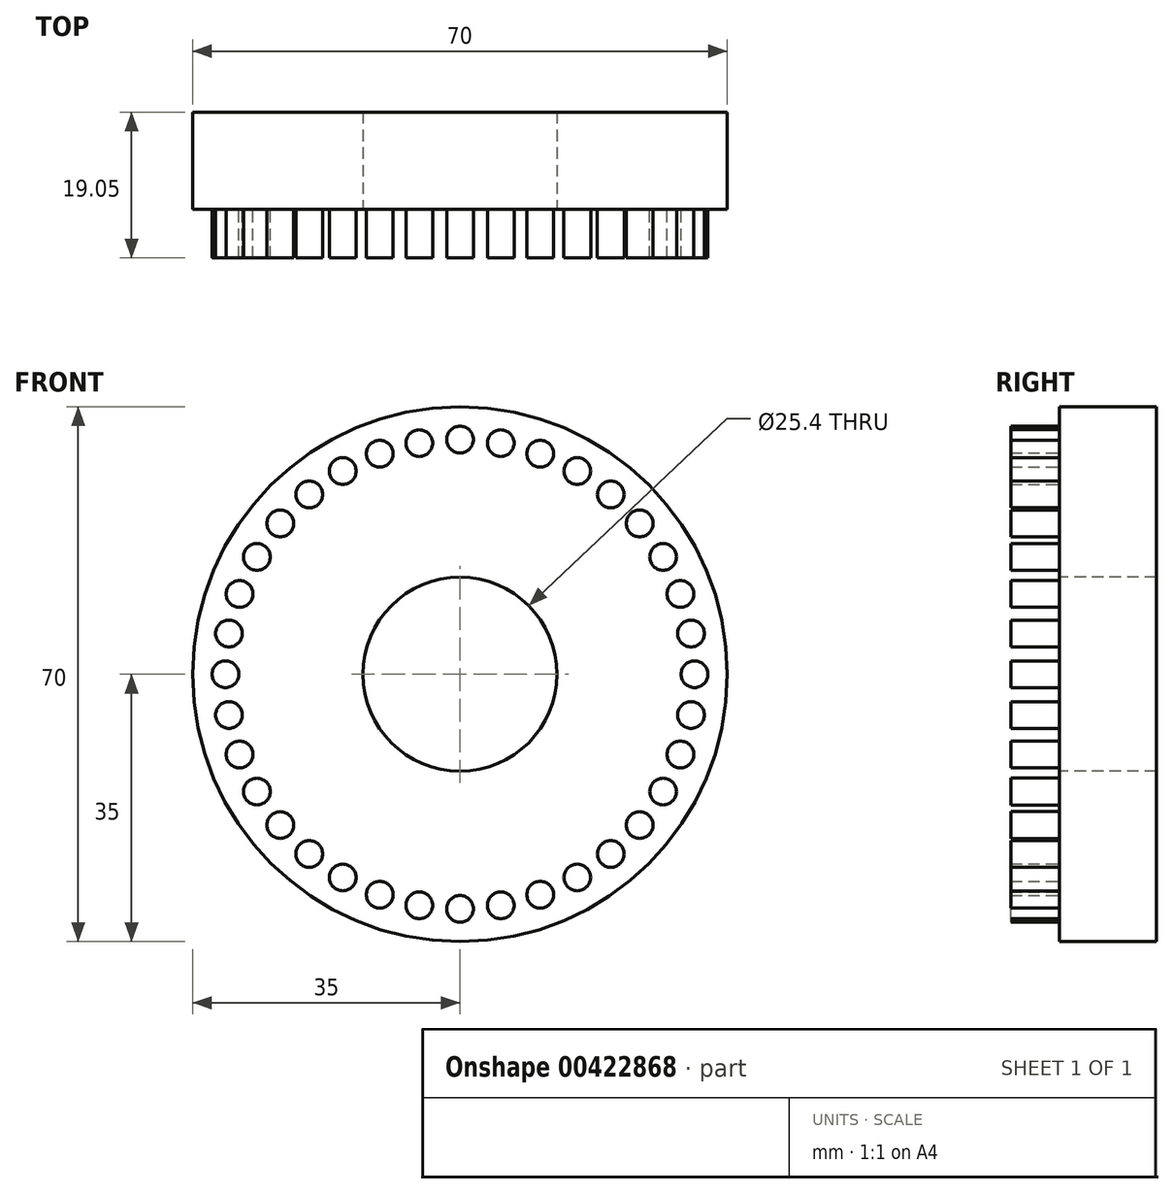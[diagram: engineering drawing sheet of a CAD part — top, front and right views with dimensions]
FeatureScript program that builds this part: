
annotation { "Feature Type Name" : "Feature", "Feature Type Description" : "" }
export const myFeature = defineFeature(function(context is Context, id is Id, definition is map)
    precondition{}
    {
        {
            var Q0;
            Q0=qCreatedBy(makeId("Front.planeOp"),FACE);
            var sketch = newSketch(context, id + "F0", { "sketchPlane" : qUnion([Q0])});
            skCircle(sketch, "E0", {"center": v(0, 0) * mm, "radius": 35 * mm});
            skSolve(sketch);
        }
        {
            var Q0;
            Q0=makeQuery(id+"F0.imprint","IMPRINT",FACE,{"disambiguationData":[TD([[makeQuery(id+"F0.imprint","IMPRINT",EDGE,{"derivedFrom":sQuery(id+"F0.wireOp",EDGE,"E0")}),1.0]])]});
            var Q1;
            Q1=sQuery(id+"F0.wireOp",EDGE,"E0");
            extrude(context, id + "F1", {"entities" : qUnion([Q0]), "surfaceEntities" : qUnion([Q1]), "depth" : 12.7 * mm});
        }
        {
            var Q0;
            Q0=makeQuery(id+"F1.opExtrude","CAP_FACE",FACE,{"disambiguationData":[OSD([sQuery(id+"F0.wireOp",EDGE,"E0")])],"isStart":false});
            var sketch = newSketch(context, id + "F2", { "sketchPlane" : qUnion([Q0])});
            skCircle(sketch, "E1", {"center": v(-30.7, 0) * mm, "radius": 1.75 * mm});
            skCircle(sketch, "E2.1.0", {"center": v(-30.24, 5.33) * mm, "radius": 1.75 * mm});
            skCircle(sketch, "E2.2.0", {"center": v(-28.86, 10.5) * mm, "radius": 1.75 * mm});
            skCircle(sketch, "E2.3.0", {"center": v(-26.6, 15.35) * mm, "radius": 1.75 * mm});
            skCircle(sketch, "E2.4.0", {"center": v(-23.52, 19.74) * mm, "radius": 1.75 * mm});
            skCircle(sketch, "E2.5.0", {"center": v(-19.74, 23.52) * mm, "radius": 1.75 * mm});
            skCircle(sketch, "E2.6.0", {"center": v(-15.35, 26.6) * mm, "radius": 1.75 * mm});
            skCircle(sketch, "E2.7.0", {"center": v(-10.5, 28.86) * mm, "radius": 1.75 * mm});
            skCircle(sketch, "E2.8.0", {"center": v(-5.33, 30.24) * mm, "radius": 1.75 * mm});
            skCircle(sketch, "E2.9.0", {"center": v(0, 30.7) * mm, "radius": 1.75 * mm});
            skPoint(sketch, "E2.center", {"position": v(0, 0) * mm});
            skLineSegment(sketch, "E2.anchor1", {"start": v(0, 0) * mm, "end": v(-30.7, 0) * mm, "construction": true});
            skLineSegment(sketch, "E2.anchor2", {"start": v(0, 0) * mm, "end": v(-30.24, -5.33) * mm, "construction": true});
            skCircle(sketch, "E3.1.10.0", {"center": v(5.33, 30.24) * mm, "radius": 1.75 * mm});
            skCircle(sketch, "E3.1.11.0", {"center": v(10.5, 28.86) * mm, "radius": 1.75 * mm});
            skCircle(sketch, "E4.1.12.0", {"center": v(15.35, 26.6) * mm, "radius": 1.75 * mm});
            skCircle(sketch, "E4.1.13.0", {"center": v(19.74, 23.52) * mm, "radius": 1.75 * mm});
            skCircle(sketch, "E4.1.14.0", {"center": v(23.52, 19.74) * mm, "radius": 1.75 * mm});
            skCircle(sketch, "E4.1.15.0", {"center": v(26.6, 15.35) * mm, "radius": 1.75 * mm});
            skCircle(sketch, "E4.1.16.0", {"center": v(28.86, 10.5) * mm, "radius": 1.75 * mm});
            skCircle(sketch, "E4.1.17.0", {"center": v(30.24, 5.33) * mm, "radius": 1.75 * mm});
            skCircle(sketch, "E4.1.18.0", {"center": v(30.7, 0) * mm, "radius": 1.75 * mm});
            skCircle(sketch, "E4.1.19.0", {"center": v(30.24, -5.33) * mm, "radius": 1.75 * mm});
            skCircle(sketch, "E4.1.20.0", {"center": v(28.86, -10.5) * mm, "radius": 1.75 * mm});
            skCircle(sketch, "E4.1.21.0", {"center": v(26.6, -15.35) * mm, "radius": 1.75 * mm});
            skCircle(sketch, "E4.1.22.0", {"center": v(23.52, -19.74) * mm, "radius": 1.75 * mm});
            skCircle(sketch, "E4.1.23.0", {"center": v(19.74, -23.52) * mm, "radius": 1.75 * mm});
            skCircle(sketch, "E4.1.24.0", {"center": v(15.35, -26.6) * mm, "radius": 1.75 * mm});
            skCircle(sketch, "E4.1.25.0", {"center": v(10.5, -28.86) * mm, "radius": 1.75 * mm});
            skCircle(sketch, "E4.1.26.0", {"center": v(5.33, -30.24) * mm, "radius": 1.75 * mm});
            skCircle(sketch, "E4.1.27.0", {"center": v(0, -30.7) * mm, "radius": 1.75 * mm});
            skCircle(sketch, "E4.1.28.0", {"center": v(-5.33, -30.24) * mm, "radius": 1.75 * mm});
            skCircle(sketch, "E4.1.29.0", {"center": v(-10.5, -28.86) * mm, "radius": 1.75 * mm});
            skCircle(sketch, "E4.1.30.0", {"center": v(-15.35, -26.6) * mm, "radius": 1.75 * mm});
            skCircle(sketch, "E4.1.31.0", {"center": v(-19.74, -23.52) * mm, "radius": 1.75 * mm});
            skCircle(sketch, "E4.1.32.0", {"center": v(-23.52, -19.74) * mm, "radius": 1.75 * mm});
            skCircle(sketch, "E4.1.33.0", {"center": v(-26.6, -15.35) * mm, "radius": 1.75 * mm});
            skCircle(sketch, "E4.1.34.0", {"center": v(-28.86, -10.5) * mm, "radius": 1.75 * mm});
            skCircle(sketch, "E4.1.35.0", {"center": v(-30.24, -5.33) * mm, "radius": 1.75 * mm});
            skSolve(sketch);
        }
        {
            var Q0;
            Q0 = qSketchRegion(id + "F2", true);
            extrude(context, id + "F3", {"entities" : qUnion([Q0]), "operationType" : NewBodyOperationType.ADD, "depth" : 6.35 * mm});
        }
        {
            var Q0;
            Q0=makeQuery(id+"F1.opExtrude","CAP_FACE",FACE,{"disambiguationData":[OSD([sQuery(id+"F0.wireOp",EDGE,"E0")])],"isStart":false});
            var sketch = newSketch(context, id + "F4", { "sketchPlane" : qUnion([Q0])});
            skCircle(sketch, "E5", {"center": v(0, 0) * mm, "radius": 12.7 * mm});
            skSolve(sketch);
        }
        {
            var Q0;
            Q0 = qSketchRegion(id + "F4", true);
            extrude(context, id + "F5", {"entities" : qUnion([Q0]), "operationType" : NewBodyOperationType.REMOVE, "endBound" : BoundingType.THROUGH_ALL, "oppositeDirection" : true, "depth" : 25.4 * mm});
        }
    });
